# Revit family: Urinal-Flush_Actuator_Sensor-KOHLER-Summon-K-29182T
name_source: partatom
category: Plumbing Fixtures
units: mm (PartAtom-declared; Revit-internal decimal feet)

## family parameters
Cut with Voids When Loaded = No
Host = Face
OmniClass Number = 23.31.25.00
OmniClass Title = Toilet and Bath Specialties
Part Type = Normal
Room Calculation Point = No
Round Connector Dimension = Use Diameter
Shared = No

## types (6) — shared parameters
ADA Compliant = No
Apparent Load = 0 VA
Assembly Code = D2020
CW Connection = Yes
Cold Water Inlet = Cold Water Inlet
Cold Water Outlet = Cold Water Outlet
Date Modified = 08/08/2022
Default Elevation = 36"
Electrical Connector = Yes
Electrical Note = One Dedicated Circuit Required
Finish = Kohler-Glass-7-Black_Black
Flow Rate = 0 GPM
HW Connection = No
Height = 6 1/4"
Hot Water Inlet = Hot Water Inlet
Length = 3/16"
Manufacturer = Kohler Co.
Master Format 2014 = 23 09 13.33
Master Format 2014 Name = Control Valves
Material = Glass
Pressure = 80.00 psi
Product Name = Summon
URL = http://www.kohler.com.cn
Vent Connection = No
Voltage = 220 V
Waste Connection = No
Waste Water Outlet = Waste Water Outlet
WaterSense Certified = No
Width = 6 1/4"

## per-type parameters (varying)
| type | Description | Flush Rate- LPF | Model | Type |
| 3LPF,7-Black | Toilet Sensor, 3L/4.5L&6L | 3LPF | K-29182T-7 | 1 |
| 4.5LPF,7-Black | Toilet Sensor, 3L/4.5L&6L | 4.5LPF | K-29182T-7 | 2 |
| 6LPF,7-Black | Toilet Sensor, 3L/4.5L&6L | 6LPF | K-29182T-7 | 3 |
| 3LPF-IOT,7-Black | Toilet Sensor, 3L/4.5L&6L-Internet Of Things | 3LPF | K-29182T-X-7 | 4 |
| 4.5LPF-IOT,7-Black | Toilet Sensor, 3L/4.5L&6L-Internet Of Things | 4.5LPF | K-29182T-X-7 | 5 |
| 6LPF-IOT,7-Black | Toilet Sensor, 3L/4.5L&6L-Internet Of Things | 6LPF | K-29182T-X-7 | 6 |

## geometry (parser evidence)
native form markers: Sweep x6
no freeform markers — native parametric forms only
